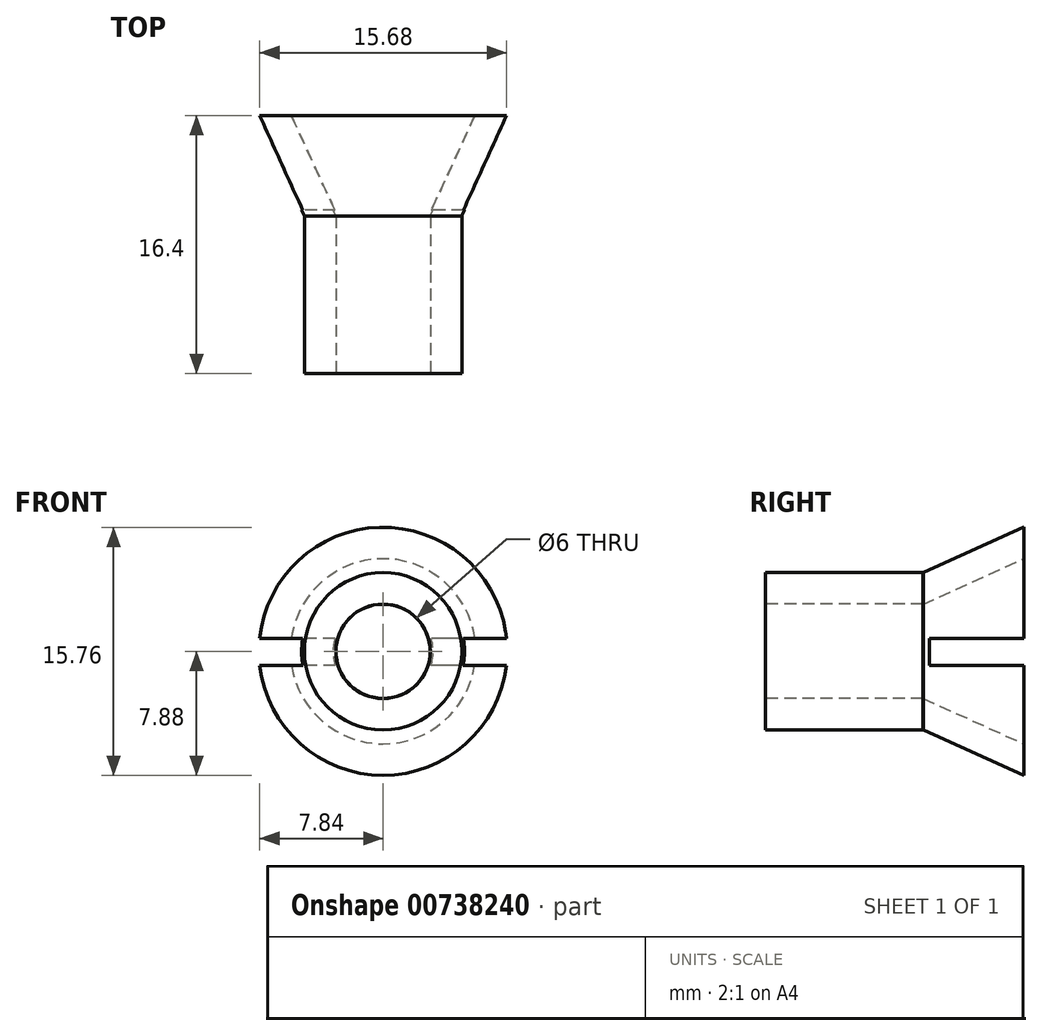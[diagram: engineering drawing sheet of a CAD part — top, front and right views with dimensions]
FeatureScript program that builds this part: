
annotation { "Feature Type Name" : "Feature", "Feature Type Description" : "" }
export const myFeature = defineFeature(function(context is Context, id is Id, definition is map)
    precondition{}
    {
        {
            var Q0;
            Q0=qCreatedBy(makeId("Front.planeOp"),FACE);
            var sketch = newSketch(context, id + "F0", { "sketchPlane" : qUnion([Q0])});
            skCircle(sketch, "E0", {"center": v(0, 0) * mm, "radius": 5 * mm});
            skCircle(sketch, "E1", {"center": v(0, 0) * mm, "radius": 3 * mm});
            skSolve(sketch);
        }
        {
            var Q0;
            Q0 = qSketchRegion(id + "F0", true);
            extrude(context, id + "F1", {"entities" : qUnion([Q0]), "oppositeDirection" : true, "depth" : 10 * mm, "offsetDistance" : 25 * mm});
        }
        {
            var Q0;
            Q0=makeQuery(id+"F1.opExtrude","CAP_FACE",FACE,{"disambiguationData":[OSD([sQuery(id+"F0.wireOp",EDGE,"E0"),sQuery(id+"F0.wireOp",EDGE,"E1")])],"isStart":true});
            var sketch = newSketch(context, id + "F2", { "sketchPlane" : qUnion([Q0])});
            skCircle(sketch, "E2", {"center": v(0, 0) * mm, "radius": 5 * mm});
            skCircle(sketch, "E3", {"center": v(0, 0) * mm, "radius": 3 * mm});
            skSolve(sketch);
        }
        {
            var Q0;
            Q0=qCreatedBy(makeId("Top.planeOp"),FACE);
            var sketch = newSketch(context, id + "F3", { "sketchPlane" : qUnion([Q0])});
            skLineSegment(sketch, "E4", {"start": v(5, 10.02) * mm, "end": v(7.88, 16.4) * mm});
            skLineSegment(sketch, "E5", {"start": v(7.88, 16.4) * mm, "end": v(5.88, 16.4) * mm});
            skLineSegment(sketch, "E6", {"start": v(5.88, 16.4) * mm, "end": v(3, 10.01) * mm});
            skLineSegment(sketch, "E7", {"start": v(3, 10.01) * mm, "end": v(5, 10.02) * mm});
            skLineSegment(sketch, "E8", {"start": v(0, 10.03) * mm, "end": v(0, 22.04) * mm});
            skSolve(sketch);
        }
        {
            var Q0;
            Q0 = qSketchRegion(id + "F3", true);
            var Q1;
            Q1=sQuery(id+"F3.wireOp",EDGE,"E8");
            revolve(context, id + "F4", {"surfaceOperationType" : NewSurfaceOperationType.NEW, "entities" : qUnion([Q0]), "axis" : qUnion([Q1]), "revolveType" : RevolveType.FULL});
        }
        {
            var Q0;
            Q0=makeQuery(id+"F4.opRevolve","SWEPT_FACE",FACE,{"disambiguationData":[OSD([sQuery(id+"F3.wireOp",EDGE,"E5")])]});
            var sketch = newSketch(context, id + "F5", { "sketchPlane" : qUnion([Q0])});
            skLineSegment(sketch, "E9.bottom", {"start": v(-8.8, 0.81) * mm, "end": v(9.34, 0.81) * mm});
            skLineSegment(sketch, "E9.top", {"start": v(-8.8, -0.89) * mm, "end": v(9.34, -0.89) * mm});
            skLineSegment(sketch, "E9.left", {"start": v(-8.8, 0.81) * mm, "end": v(-8.8, -0.89) * mm});
            skLineSegment(sketch, "E9.right", {"start": v(9.34, 0.81) * mm, "end": v(9.34, -0.89) * mm});
            skSolve(sketch);
        }
        {
            var Q0;
            {var subQ0=sQuery(id+"F5.wireOp",EDGE,"E9.bottom");var subQ1=sQuery(id+"F3.wireOp",EDGE,"E5");var subQ2=makeQuery(id+"F4.opRevolve","SWEPT_EDGE",EDGE,{"disambiguationData":[OSD([sQuery(id+"F3.wireOp",EDGE,"E4"),subQ1])]});var subQ3=makeQuery(id+"F5.imprint","INTERSECT",VERTEX,{"disambiguationData":[OD(0.0)],"derivedFrom":[subQ2,subQ0]});Q0=makeQuery(id+"F5.imprint","IMPRINT",FACE,{"disambiguationData":[TD([[makeQuery(id+"F5.imprint","IMPRINT",EDGE,{"disambiguationData":[TD([[subQ3,-1.0]])],"derivedFrom":subQ0}),-1.0]])]});}
            var Q1;
            {var subQ0=sQuery(id+"F5.wireOp",EDGE,"E9.right");Q1=makeQuery(id+"F5.imprint","IMPRINT",FACE,{"disambiguationData":[TD([[makeQuery(id+"F5.imprint","IMPRINT",EDGE,{"derivedFrom":subQ0}),-1.0]])]});}
            var Q2;
            {var subQ0=sQuery(id+"F5.wireOp",EDGE,"E9.bottom");var subQ1=makeQuery(id+"F4.opRevolve","SWEPT_EDGE",EDGE,{"disambiguationData":[OSD([sQuery(id+"F3.wireOp",EDGE,"E5"),sQuery(id+"F3.wireOp",EDGE,"E6")])]});var subQ2=makeQuery(id+"F5.imprint","INTERSECT",VERTEX,{"disambiguationData":[OD(0.0)],"derivedFrom":[subQ1,subQ0]});Q2=makeQuery(id+"F5.imprint","IMPRINT",FACE,{"disambiguationData":[TD([[makeQuery(id+"F5.imprint","IMPRINT",EDGE,{"disambiguationData":[TD([[subQ2,-1.0]])],"derivedFrom":subQ0}),-1.0]])]});}
            var Q3;
            {var subQ0=sQuery(id+"F5.wireOp",EDGE,"E9.bottom");var subQ1=sQuery(id+"F3.wireOp",EDGE,"E5");var subQ2=makeQuery(id+"F4.opRevolve","SWEPT_EDGE",EDGE,{"disambiguationData":[OSD([sQuery(id+"F3.wireOp",EDGE,"E4"),subQ1])]});var subQ3=makeQuery(id+"F5.imprint","INTERSECT",VERTEX,{"disambiguationData":[OD(1.0)],"derivedFrom":[subQ2,subQ0]});Q3=makeQuery(id+"F5.imprint","IMPRINT",FACE,{"disambiguationData":[TD([[makeQuery(id+"F5.imprint","IMPRINT",EDGE,{"disambiguationData":[TD([[subQ3,1.0]])],"derivedFrom":subQ0}),-1.0]])]});}
            var Q4;
            {var subQ0=sQuery(id+"F5.wireOp",EDGE,"E9.left");Q4=makeQuery(id+"F5.imprint","IMPRINT",FACE,{"disambiguationData":[TD([[makeQuery(id+"F5.imprint","IMPRINT",EDGE,{"derivedFrom":subQ0}),1.0]])]});}
            var Q5;
            Q5=sQuery(id+"F5.wireOp",EDGE,"E9.bottom");
            var Q6;
            Q6=sQuery(id+"F5.wireOp",EDGE,"E9.top");
            var Q7;
            Q7=sQuery(id+"F5.wireOp",EDGE,"E9.left");
            var Q8;
            Q8=sQuery(id+"F5.wireOp",EDGE,"E9.right");
            extrude(context, id + "F6", {"entities" : qUnion([Q0, Q1, Q2, Q3, Q4]), "operationType" : NewBodyOperationType.REMOVE, "surfaceEntities" : qUnion([Q5, Q6, Q7, Q8]), "oppositeDirection" : true, "depth" : 6 * mm, "offsetDistance" : 25 * mm});
        }
    });
